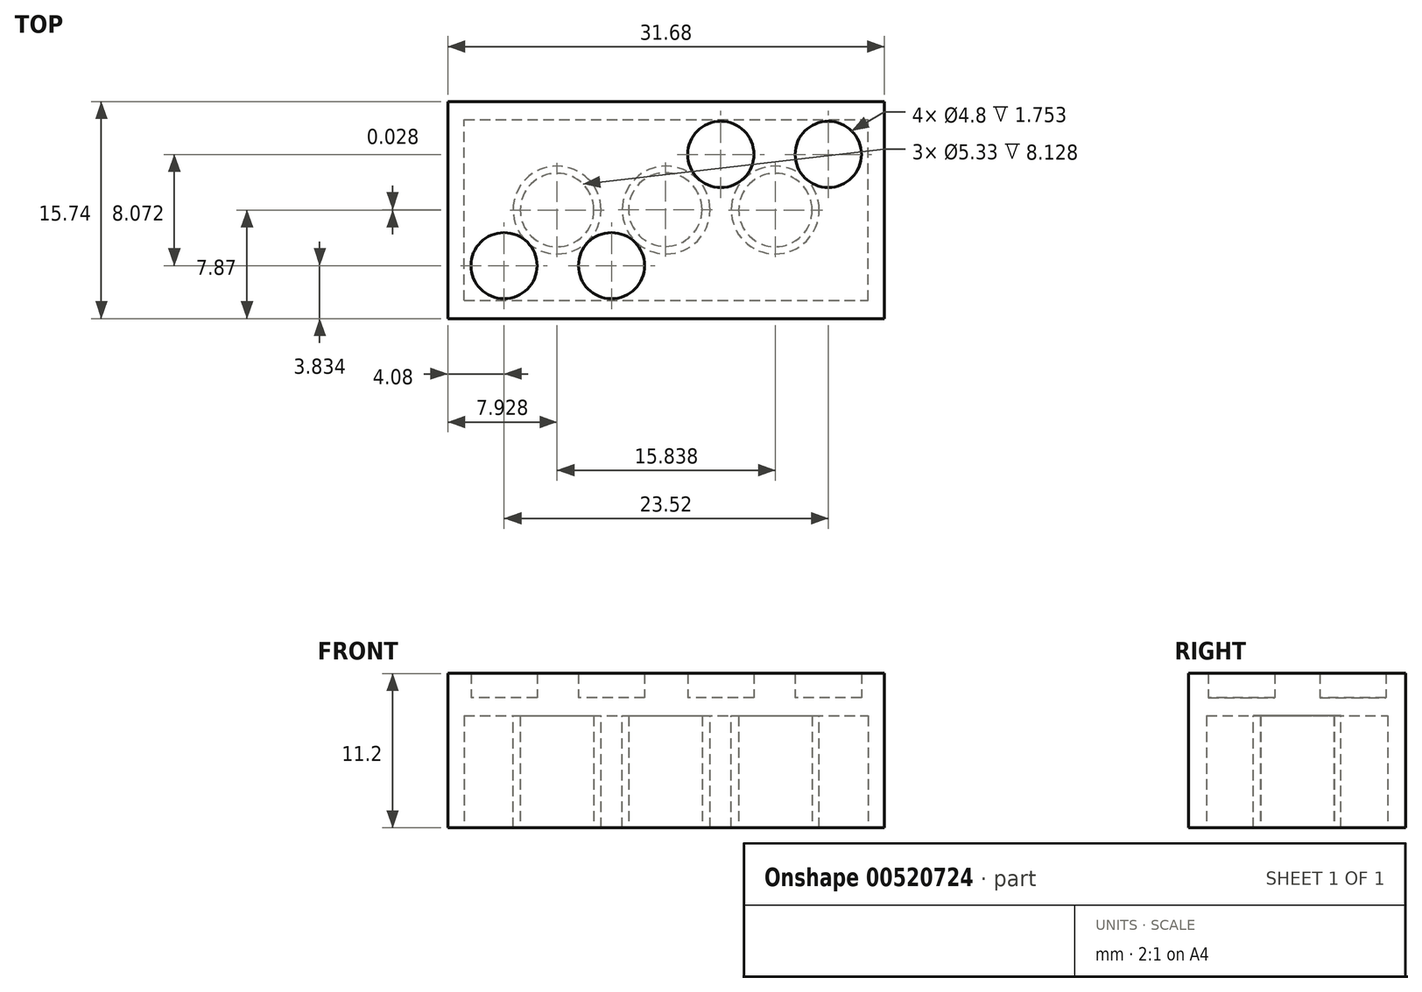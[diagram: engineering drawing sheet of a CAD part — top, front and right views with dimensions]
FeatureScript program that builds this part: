
annotation { "Feature Type Name" : "Feature", "Feature Type Description" : "" }
export const myFeature = defineFeature(function(context is Context, id is Id, definition is map)
    precondition{}
    {
        {
            var Q0;
            Q0=qCreatedBy(makeId("Top.planeOp"),FACE);
            var sketch = newSketch(context, id + "F0", { "sketchPlane" : qUnion([Q0])});
            skLineSegment(sketch, "E0.bottom", {"start": v(-15.84, 7.87) * mm, "end": v(15.84, 7.87) * mm});
            skLineSegment(sketch, "E0.top", {"start": v(-15.84, -7.87) * mm, "end": v(15.84, -7.87) * mm});
            skLineSegment(sketch, "E0.left", {"start": v(-15.84, 7.87) * mm, "end": v(-15.84, -7.87) * mm});
            skLineSegment(sketch, "E0.right", {"start": v(15.84, 7.87) * mm, "end": v(15.84, -7.87) * mm});
            skPoint(sketch, "E0.middle", {"position": v(0, 0) * mm});
            skSolve(sketch);
        }
        {
            var Q0;
            Q0=makeQuery(id+"F0.imprint","IMPRINT",FACE,{"disambiguationData":[TD([[makeQuery(id+"F0.imprint","IMPRINT",EDGE,{"derivedFrom":sQuery(id+"F0.wireOp",EDGE,"E0.bottom")}),-1.0]])]});
            extrude(context, id + "F1", {"entities" : qUnion([Q0]), "depth" : 9.45 * mm, "offsetDistance" : 25.4 * mm});
        }
        {
            var Q0;
            Q0=makeQuery(id+"F1.opExtrude","CAP_FACE",FACE,{"disambiguationData":[OSD([sQuery(id+"F0.wireOp",EDGE,"E0.bottom"),sQuery(id+"F0.wireOp",EDGE,"E0.top"),sQuery(id+"F0.wireOp",EDGE,"E0.left"),sQuery(id+"F0.wireOp",EDGE,"E0.right")])],"isStart":false});
            var sketch = newSketch(context, id + "F2", { "sketchPlane" : qUnion([Q0])});
            skCircle(sketch, "E1", {"center": v(-11.76, 4.04) * mm, "radius": 2.4 * mm});
            skCircle(sketch, "E2", {"center": v(-3.96, 4.04) * mm, "radius": 2.4 * mm});
            skCircle(sketch, "E3.MirrorC", {"center": v(3.96, 4.04) * mm, "radius": 2.4 * mm});
            skCircle(sketch, "E4.MirrorC", {"center": v(11.76, 4.04) * mm, "radius": 2.4 * mm});
            skCircle(sketch, "E5.MirrorC", {"center": v(11.76, -4.04) * mm, "radius": 2.4 * mm});
            skCircle(sketch, "E6.MirrorC", {"center": v(3.96, -4.04) * mm, "radius": 2.4 * mm});
            skCircle(sketch, "E7.MirrorC", {"center": v(-3.96, -4.04) * mm, "radius": 2.4 * mm});
            skCircle(sketch, "E8.MirrorC", {"center": v(-11.76, -4.04) * mm, "radius": 2.4 * mm});
            skSolve(sketch);
        }
        {
            var Q0;
            Q0=makeQuery(id+"F2.imprint","IMPRINT",FACE,{"disambiguationData":[TD([[makeQuery(id+"F2.imprint","IMPRINT",EDGE,{"derivedFrom":sQuery(id+"F2.wireOp",EDGE,"E1")}),1.0]])]});
            var Q1;
            Q1=makeQuery(id+"F2.imprint","IMPRINT",FACE,{"disambiguationData":[TD([[makeQuery(id+"F2.imprint","IMPRINT",EDGE,{"derivedFrom":sQuery(id+"F2.wireOp",EDGE,"E6.MirrorC")}),1.0]])]});
            var Q2;
            Q2=makeQuery(id+"F2.imprint","IMPRINT",FACE,{"disambiguationData":[TD([[makeQuery(id+"F2.imprint","IMPRINT",EDGE,{"derivedFrom":sQuery(id+"F2.wireOp",EDGE,"E3.MirrorC")}),-1.0]])]});
            var Q3;
            Q3=makeQuery(id+"F2.imprint","IMPRINT",FACE,{"disambiguationData":[TD([[makeQuery(id+"F2.imprint","IMPRINT",EDGE,{"derivedFrom":sQuery(id+"F2.wireOp",EDGE,"E2")}),1.0]])]});
            var Q4;
            Q4=makeQuery(id+"F2.imprint","IMPRINT",FACE,{"disambiguationData":[TD([[makeQuery(id+"F2.imprint","IMPRINT",EDGE,{"derivedFrom":sQuery(id+"F2.wireOp",EDGE,"E7.MirrorC")}),-1.0]])]});
            var Q5;
            Q5=makeQuery(id+"F2.imprint","IMPRINT",FACE,{"disambiguationData":[TD([[makeQuery(id+"F2.imprint","IMPRINT",EDGE,{"derivedFrom":sQuery(id+"F2.wireOp",EDGE,"E8.MirrorC")}),-1.0]])]});
            var Q6;
            Q6=makeQuery(id+"F2.imprint","IMPRINT",FACE,{"disambiguationData":[TD([[makeQuery(id+"F2.imprint","IMPRINT",EDGE,{"derivedFrom":sQuery(id+"F2.wireOp",EDGE,"E5.MirrorC")}),1.0]])]});
            var Q7;
            Q7=makeQuery(id+"F2.imprint","IMPRINT",FACE,{"disambiguationData":[TD([[makeQuery(id+"F2.imprint","IMPRINT",EDGE,{"derivedFrom":sQuery(id+"F2.wireOp",EDGE,"E4.MirrorC")}),-1.0]])]});
            extrude(context, id + "F3", {"entities" : qUnion([Q0, Q1, Q2, Q3, Q4, Q5, Q6, Q7]), "operationType" : NewBodyOperationType.ADD, "depth" : 1.75 * mm, "offsetDistance" : 25.4 * mm});
        }
        {
            var Q0;
            Q0=makeQuery(id+"F1.opExtrude","CAP_FACE",FACE,{"disambiguationData":[OSD([sQuery(id+"F0.wireOp",EDGE,"E0.bottom"),sQuery(id+"F0.wireOp",EDGE,"E0.top"),sQuery(id+"F0.wireOp",EDGE,"E0.left"),sQuery(id+"F0.wireOp",EDGE,"E0.right")])],"isStart":true});
            var sketch = newSketch(context, id + "F4", { "sketchPlane" : qUnion([Q0])});
            skLineSegment(sketch, "E9.bottom", {"start": v(-14.66, 6.57) * mm, "end": v(14.66, 6.57) * mm});
            skLineSegment(sketch, "E9.top", {"start": v(-14.66, -6.57) * mm, "end": v(14.66, -6.57) * mm});
            skLineSegment(sketch, "E9.left", {"start": v(-14.66, 6.57) * mm, "end": v(-14.66, -6.57) * mm});
            skLineSegment(sketch, "E9.right", {"start": v(14.66, 6.57) * mm, "end": v(14.66, -6.57) * mm});
            skPoint(sketch, "E9.middle", {"position": v(0, 0) * mm});
            skSolve(sketch);
        }
        {
            var Q0;
            Q0=makeQuery(id+"F4.imprint","IMPRINT",FACE,{"disambiguationData":[TD([[makeQuery(id+"F4.imprint","IMPRINT",EDGE,{"derivedFrom":sQuery(id+"F4.wireOp",EDGE,"E9.bottom")}),-1.0]])]});
            extrude(context, id + "F5", {"entities" : qUnion([Q0]), "operationType" : NewBodyOperationType.REMOVE, "oppositeDirection" : true, "depth" : 8.13 * mm, "offsetDistance" : 25.4 * mm});
        }
        {
            var Q0;
            Q0=makeQuery(id+"F5.boolean.opBoolean","COPY",FACE,{"derivedFrom":makeQuery(id+"F5.opExtrude","CAP_FACE",FACE,{"disambiguationData":[OSD([sQuery(id+"F4.wireOp",EDGE,"E9.bottom"),sQuery(id+"F4.wireOp",EDGE,"E9.top"),sQuery(id+"F4.wireOp",EDGE,"E9.left"),sQuery(id+"F4.wireOp",EDGE,"E9.right")])],"isStart":false})});
            var sketch = newSketch(context, id + "F6", { "sketchPlane" : qUnion([Q0])});
            skCircle(sketch, "E10", {"center": v(-7.91, 0) * mm, "radius": 3.19 * mm});
            skCircle(sketch, "E11", {"center": v(0, 0) * mm, "radius": 3.19 * mm});
            skCircle(sketch, "E12", {"center": v(7.91, 0) * mm, "radius": 3.19 * mm});
            skSolve(sketch);
        }
        {
            var Q0;
            Q0=makeQuery(id+"F6.imprint","IMPRINT",FACE,{"disambiguationData":[TD([[makeQuery(id+"F6.imprint","IMPRINT",EDGE,{"derivedFrom":sQuery(id+"F6.wireOp",EDGE,"E10")}),1.0]])]});
            var Q1;
            Q1=makeQuery(id+"F6.imprint","IMPRINT",FACE,{"disambiguationData":[TD([[makeQuery(id+"F6.imprint","IMPRINT",EDGE,{"derivedFrom":sQuery(id+"F6.wireOp",EDGE,"E12")}),1.0]])]});
            var Q2;
            Q2=makeQuery(id+"F6.imprint","IMPRINT",FACE,{"disambiguationData":[TD([[makeQuery(id+"F6.imprint","IMPRINT",EDGE,{"derivedFrom":sQuery(id+"F6.wireOp",EDGE,"E11")}),1.0]])]});
            extrude(context, id + "F7", {"entities" : qUnion([Q0, Q1, Q2]), "operationType" : NewBodyOperationType.ADD, "depth" : 8.13 * mm, "offsetDistance" : 25.4 * mm});
        }
        {
            var Q0;
            Q0=makeQuery(id+"F7.opExtrude","CAP_FACE",FACE,{"disambiguationData":[OSD([sQuery(id+"F6.wireOp",EDGE,"E10")])],"isStart":false});
            var sketch = newSketch(context, id + "F8", { "sketchPlane" : qUnion([Q0])});
            skCircle(sketch, "E13", {"center": v(-7.91, 0) * mm, "radius": 2.67 * mm});
            skCircle(sketch, "E14", {"center": v(-0.06, -0.03) * mm, "radius": 2.67 * mm});
            skCircle(sketch, "E15", {"center": v(7.93, 0) * mm, "radius": 2.67 * mm});
            skSolve(sketch);
        }
        {
            var Q0;
            Q0=makeQuery(id+"F8.imprint","IMPRINT",FACE,{"disambiguationData":[TD([[makeQuery(id+"F8.imprint","IMPRINT",EDGE,{"derivedFrom":sQuery(id+"F8.wireOp",EDGE,"E13")}),1.0]])]});
            var Q1;
            Q1=makeQuery(id+"F8.imprint","IMPRINT",FACE,{"disambiguationData":[TD([[makeQuery(id+"F8.imprint","IMPRINT",EDGE,{"derivedFrom":sQuery(id+"F8.wireOp",EDGE,"E14")}),1.0]])]});
            var Q2;
            Q2=makeQuery(id+"F8.imprint","IMPRINT",FACE,{"disambiguationData":[TD([[makeQuery(id+"F8.imprint","IMPRINT",EDGE,{"derivedFrom":sQuery(id+"F8.wireOp",EDGE,"E15")}),1.0]])]});
            extrude(context, id + "F9", {"entities" : qUnion([Q0, Q1, Q2]), "operationType" : NewBodyOperationType.REMOVE, "oppositeDirection" : true, "depth" : 8.13 * mm, "offsetDistance" : 25.4 * mm});
        }
    });
